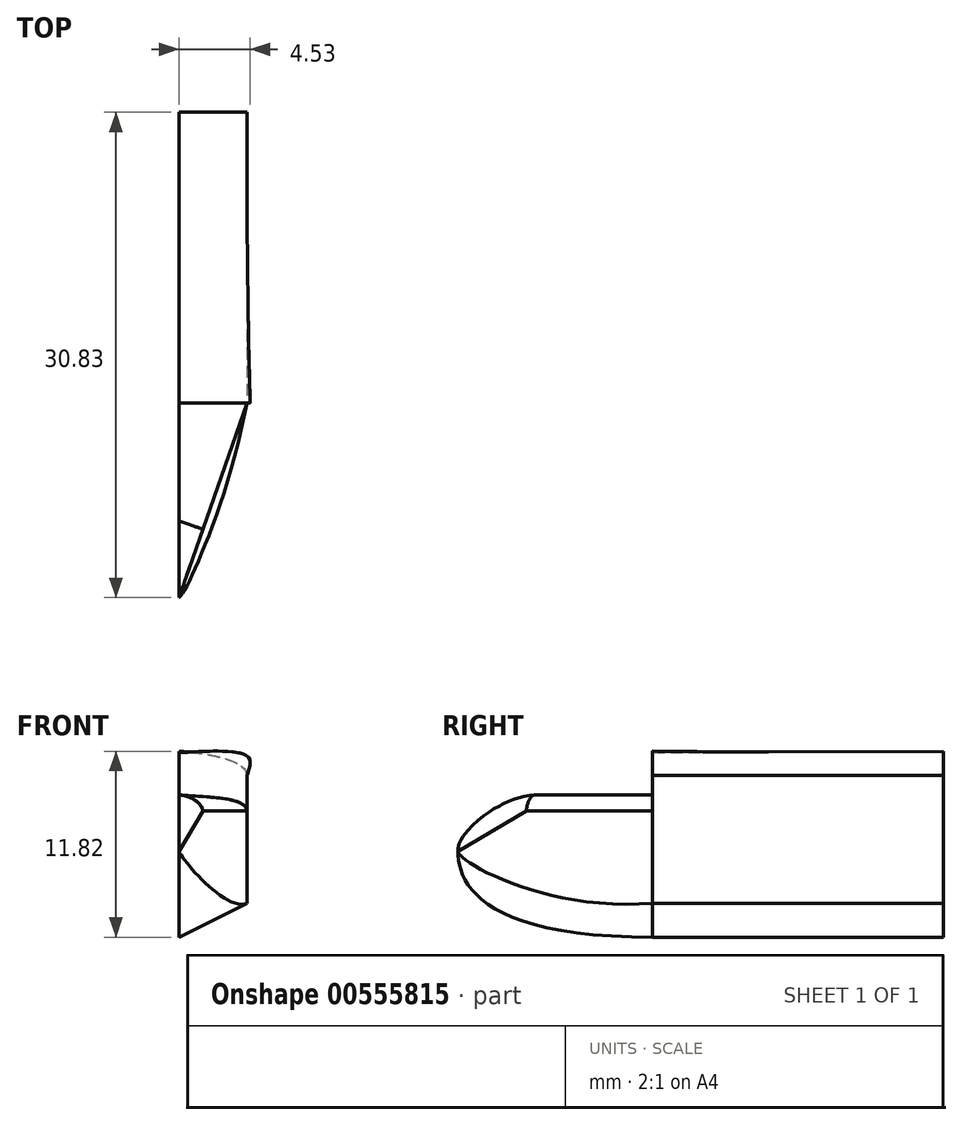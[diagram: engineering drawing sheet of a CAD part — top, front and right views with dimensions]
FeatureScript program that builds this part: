
annotation { "Feature Type Name" : "Feature", "Feature Type Description" : "" }
export const myFeature = defineFeature(function(context is Context, id is Id, definition is map)
    precondition{}
    {
        {
            var Q0;
            Q0=qCreatedBy(makeId("Right.planeOp"),FACE);
            var sketch = newSketch(context, id + "F0", { "sketchPlane" : qUnion([Q0])});
            skLineSegment(sketch, "E0.bottom", {"start": v(-49.13, 14.56) * mm, "end": v(-30.67, 14.56) * mm});
            skLineSegment(sketch, "E0.top", {"start": v(-49.13, 2.76) * mm, "end": v(-30.67, 2.76) * mm});
            skLineSegment(sketch, "E0.left", {"start": v(-49.13, 14.56) * mm, "end": v(-49.13, 2.76) * mm});
            skLineSegment(sketch, "E0.right", {"start": v(-30.67, 14.56) * mm, "end": v(-30.67, 2.76) * mm});
            skLineSegment(sketch, "E1", {"start": v(32.77, 35.45) * mm, "end": v(32.77, -92.3) * mm, "construction": true});
            skLineSegment(sketch, "E2.bottom", {"start": v(32.77, 35.45) * mm, "end": v(-64.37, 35.45) * mm, "construction": true});
            skLineSegment(sketch, "E2.top", {"start": v(32.77, -92.3) * mm, "end": v(-64.37, -92.3) * mm, "construction": true});
            skLineSegment(sketch, "E2.right", {"start": v(-64.37, 35.45) * mm, "end": v(-64.37, -92.3) * mm, "construction": true});
            skLineSegment(sketch, "E3", {"start": v(-49.13, 2.76) * mm, "end": v(-49.13, -2.43) * mm, "construction": true});
            skLineSegment(sketch, "E4", {"start": v(-30.62, 8.23) * mm, "end": v(-47.08, 8.23) * mm, "construction": true});
            skLineSegment(sketch, "E5", {"start": v(-47.08, 8.23) * mm, "end": v(-50.1, 8.23) * mm, "construction": true});
            skLineSegment(sketch, "E6", {"start": v(-50.1, 8.23) * mm, "end": v(-50.1, -2.75) * mm, "construction": true});
            skLineSegment(sketch, "E7", {"start": v(-50.1, 8.23) * mm, "end": v(-53.9, 8.23) * mm, "construction": true});
            skLineSegment(sketch, "E8", {"start": v(-53.9, 8.23) * mm, "end": v(-53.9, -2.7) * mm, "construction": true});
            skLineSegment(sketch, "E9", {"start": v(-53.9, 8.23) * mm, "end": v(-56.62, 8.23) * mm, "construction": true});
            skLineSegment(sketch, "E10", {"start": v(-56.62, 8.23) * mm, "end": v(-59.33, 8.23) * mm, "construction": true});
            skLineSegment(sketch, "E11", {"start": v(-59.33, 8.23) * mm, "end": v(-59.33, -1.53) * mm, "construction": true});
            skLineSegment(sketch, "E12", {"start": v(-56.62, 8.23) * mm, "end": v(-56.62, -1.94) * mm, "construction": true});
            skLineSegment(sketch, "E13", {"start": v(-59.33, 8.23) * mm, "end": v(-61.5, 8.23) * mm, "construction": true});
            skFitSpline(sketch, "E14", {"points": [v(-61.5, 8.23) * mm, v(-49.13, 2.76) * mm], "startDerivative": vector(0, -6.22) * mm, "endDerivative": vector(32.48, 0) * mm});
            skLineSegment(sketch, "E15", {"start": v(-56.62, 11.8) * mm, "end": v(-49.13, 11.8) * mm});
            skLineSegment(sketch, "E16", {"start": v(-56.62, 8.23) * mm, "end": v(-56.62, 11.8) * mm, "construction": true});
            skFitSpline(sketch, "E17", {"points": [v(-56.62, 11.8) * mm, v(-61.5, 8.23) * mm], "startDerivative": vector(-5.3, 0) * mm, "endDerivative": vector(0, -4.44) * mm});
            skSolve(sketch);
        }
        {
            var Q0;
            Q0=qCreatedBy(makeId("Front.planeOp"),FACE);
            var Q1;
            Q1=sQuery(id+"F0.wireOp",VERTEX,"E0.top.end");
            cPlane(context, id + "F1", {"entities" : qUnion([Q0, Q1]), "cplaneType" : CPlaneType.PLANE_POINT, "offset" : 25 * mm, "width" : 150 * mm, "height" : 150 * mm});
        }
        {
            var Q0;
            Q0=qCreatedBy(id+"F1.planeOp",FACE);
            var sketch = newSketch(context, id + "F2", { "sketchPlane" : qUnion([Q0])});
            skLineSegment(sketch, "E18.0", {"start": v(0, 14.56) * mm, "end": v(0, 2.76) * mm, "construction": true});
            skFitSpline(sketch, "E19", {"points": [v(0, 14.56) * mm, v(4.32, 13.04) * mm], "startDerivative": vector(1.52, 0) * mm, "endDerivative": vector(0, -3.7) * mm});
            skLineSegment(sketch, "E20", {"start": v(4.32, 13.04) * mm, "end": v(4.32, 4.92) * mm});
            skLineSegment(sketch, "E21", {"start": v(4.32, 4.92) * mm, "end": v(0, 2.76) * mm});
            skLineSegment(sketch, "E22", {"start": v(4.32, 4.92) * mm, "end": v(0, 4.92) * mm, "construction": true});
            skSolve(sketch);
        }
        {
            var Q0;
            Q0=sQuery(id+"F0.wireOp",EDGE,"E0.left");
            cPoint(context, id + "F3", {"entities" : qUnion([Q0]), "parameter" : 0.5});
        }
        {
            var Q0;
            Q0=qCreatedBy(makeId("Front.planeOp"),FACE);
            var Q1;
            Q1 = qCreatedBy(id + "F3" ,VERTEX);
            cPlane(context, id + "F4", {"entities" : qUnion([Q0, Q1]), "cplaneType" : CPlaneType.PLANE_POINT, "offset" : 25 * mm, "width" : 150 * mm, "height" : 150 * mm});
        }
        {
            var Q0;
            Q0=qCreatedBy(id+"F4.planeOp",FACE);
            var sketch = newSketch(context, id + "F5", { "sketchPlane" : qUnion([Q0])});
            skLineSegment(sketch, "E23.0", {"start": v(4.32, 4.92) * mm, "end": v(0, 2.76) * mm});
            skLineSegment(sketch, "E24.0", {"start": v(4.32, 13.04) * mm, "end": v(4.32, 4.92) * mm});
            skFitSpline(sketch, "E25.0", {"points": [v(0, 14.51) * mm, v(0.5, 14.51) * mm, v(4.32, 14.27) * mm, v(4.32, 13.04) * mm]});
            skSolve(sketch);
        }
        {
            var Q0;
            Q0 = qSketchRegion(id + "F2", true);
            var Q1;
            Q1 = qSketchRegion(id + "F5", true);
            var Q2;
            Q2 = qConstructionFilter(qBodyType(qCreatedBy(id + "F2" ,EDGE), BodyType.WIRE), ConstructionObject.NO);
            var Q3;
            Q3 = qConstructionFilter(qBodyType(qCreatedBy(id + "F5" ,EDGE), BodyType.WIRE), ConstructionObject.NO);
            loft(context, id + "F6", {"bodyType" : ToolBodyType.SURFACE, "sheetProfilesArray" : [{ "sheetProfileEntities" : qUnion([Q0]) }, { "sheetProfileEntities" : qUnion([Q1]) }], "wireProfilesArray" : [{ "wireProfileEntities" : qUnion([Q2]) }, { "wireProfileEntities" : qUnion([Q3]) }]});
        }
        {
            var Q0;
            Q0=qCreatedBy(makeId("Front.planeOp"),FACE);
            var Q1;
            Q1=sQuery(id+"F0.wireOp",VERTEX,"E7.start");
            cPlane(context, id + "F7", {"entities" : qUnion([Q0, Q1]), "cplaneType" : CPlaneType.PLANE_POINT, "offset" : 25 * mm, "width" : 150 * mm, "height" : 150 * mm});
        }
        {
            var Q0;
            Q0=makeQuery(id+"F6.opLoft","MID_CAP_VERTEX",VERTEX,{"disambiguationData":[OSD([sQuery(id+"F5.wireOp",VERTEX,"E24.0.end")])],"capPos":1.0});
            var Q1;
            Q1=sQuery(id+"F0.wireOp",VERTEX,"E14.0.internal");
            var Q2;
            Q2=sQuery(id+"F0.wireOp",VERTEX,"E0.left.start");
            cPlane(context, id + "F8", {"entities" : qUnion([Q0, Q1, Q2]), "cplaneType" : CPlaneType.THREE_POINT, "offset" : 25 * mm, "width" : 150 * mm, "height" : 150 * mm});
        }
        {
            var Q0;
            Q0=qCreatedBy(id+"F8.planeOp",FACE);
            var sketch = newSketch(context, id + "F9", { "sketchPlane" : qUnion([Q0])});
            skPoint(sketch, "E26.0", {"position": v(-59.5, 7.5) * mm});
            skPoint(sketch, "E27.0", {"position": v(-46.87, 2.73) * mm});
            skFitSpline(sketch, "E28", {"points": [v(-59.5, 7.5) * mm, v(-46.87, 2.73) * mm], "startDerivative": vector(0, -2.26) * mm, "endDerivative": vector(20.63, 0) * mm});
            skSolve(sketch);
        }
        {
            var Q0;
            Q0=sQuery(id+"F9.wireOp",EDGE,"E28");
            var Q1;
            Q1=sQuery(id+"F0.wireOp",EDGE,"E14");
            loft(context, id + "F10", {"bodyType" : ToolBodyType.SURFACE, "wireProfilesArray" : [{ "wireProfileEntities" : qUnion([Q0]) }, { "wireProfileEntities" : qUnion([Q1]) }]});
        }
        {
            var Q0;
            Q0=qCreatedBy(id+"F4.planeOp",FACE);
            var sketch = newSketch(context, id + "F11", { "sketchPlane" : qUnion([Q0])});
            skPoint(sketch, "E29.0", {"position": v(0, 11.8) * mm});
            skLineSegment(sketch, "E30.0", {"start": v(4.32, 4.92) * mm, "end": v(4.32, 13.04) * mm, "construction": true});
            skLineSegment(sketch, "E31", {"start": v(4.32, 4.92) * mm, "end": v(4.32, 10.79) * mm});
            skFitSpline(sketch, "E32", {"points": [v(0, 11.8) * mm, v(4.32, 10.79) * mm], "startDerivative": vector(5.4, -0.45) * mm, "endDerivative": vector(0, -2.65) * mm});
            skSolve(sketch);
        }
        {
            var Q0;
            Q0=sQuery(id+"F11.wireOp",VERTEX,"E32.1.internal");
            var Q1;
            Q1=sQuery(id+"F0.wireOp",VERTEX,"E13.end");
            var Q2;
            Q2=sQuery(id+"F11.wireOp",VERTEX,"E30.0.start");
            cPlane(context, id + "F12", {"entities" : qUnion([Q0, Q1, Q2]), "cplaneType" : CPlaneType.THREE_POINT, "offset" : 25 * mm, "width" : 150 * mm, "height" : 150 * mm});
        }
        {
            var Q0;
            Q0=qCreatedBy(id+"F12.planeOp",FACE);
            var sketch = newSketch(context, id + "F13", { "sketchPlane" : qUnion([Q0])});
            skLineSegment(sketch, "E33.0", {"start": v(53.46, 8.23) * mm, "end": v(53.46, 11.8) * mm, "construction": true});
            skPoint(sketch, "E34.0", {"position": v(44.96, 10.79) * mm});
            skPoint(sketch, "E35.0", {"position": v(58.06, 8.23) * mm});
            skFitSpline(sketch, "E36.0", {"points": [v(58.06, 8.23) * mm, v(57.96, 7.54) * mm, v(51.74, 4.35) * mm, v(44.96, 4.92) * mm]});
            skLineSegment(sketch, "E37.0", {"start": v(44.96, 4.92) * mm, "end": v(44.96, 10.79) * mm});
            skLineSegment(sketch, "E38", {"start": v(44.96, 10.79) * mm, "end": v(53.46, 10.79) * mm});
            skLineSegment(sketch, "E39", {"start": v(53.46, 10.79) * mm, "end": v(58.06, 8.23) * mm});
            skSolve(sketch);
        }
        {
            var Q0;
            Q0=sQuery(id+"F0.wireOp",VERTEX,"E15.start");
            var Q1;
            Q1=sQuery(id+"F0.wireOp",VERTEX,"E10.start");
            var Q2;
            Q2=sQuery(id+"F13.wireOp",VERTEX,"E39.start");
            cPlane(context, id + "F14", {"entities" : qUnion([Q0, Q1, Q2]), "cplaneType" : CPlaneType.THREE_POINT, "offset" : 25 * mm, "width" : 150 * mm, "height" : 150 * mm});
        }
        {
            var Q0;
            Q0=qCreatedBy(id+"F14.planeOp",FACE);
            var sketch = newSketch(context, id + "F15", { "sketchPlane" : qUnion([Q0])});
            skPoint(sketch, "E40.0", {"position": v(-18.66, 11.8) * mm});
            skPoint(sketch, "E41.0", {"position": v(-20.27, 10.79) * mm});
            skFitSpline(sketch, "E42.0", {"points": [v(-16.2, 11.8) * mm, v(-17.9, 11.65) * mm, v(-20.27, 11.67) * mm, v(-20.27, 10.79) * mm], "construction": true});
            skFitSpline(sketch, "E43", {"points": [v(-18.66, 11.8) * mm, v(-20.27, 10.79) * mm], "startDerivative": vector(-2.34, 0) * mm, "endDerivative": vector(0, -1.3) * mm});
            skSolve(sketch);
        }
        {
            var Q0;
            Q0=sQuery(id+"F15.wireOp",EDGE,"E43");
            var Q1;
            Q1=sQuery(id+"F11.wireOp",EDGE,"E32");
            loft(context, id + "F16", {"bodyType" : ToolBodyType.SURFACE, "wireProfilesArray" : [{ "wireProfileEntities" : qUnion([Q0]) }, { "wireProfileEntities" : qUnion([Q1]) }]});
        }
        {
            var Q0;
            Q0=makeQuery(id+"F16.opLoft","MID_CAP_EDGE",EDGE,{"disambiguationData":[OSD([sQuery(id+"F15.wireOp",VERTEX,"E43.start"),sQuery(id+"F15.wireOp",VERTEX,"E43.end"),sQuery(id+"F15.wireOp",EDGE,"E43")])],"capPos":0.0});
            var Q1;
            Q1=sQuery(id+"F13.wireOp",VERTEX,"E35.0");
            var Q2;
            Q2=sQuery(id+"F0.wireOp",EDGE,"E17");
            loft(context, id + "F17", {"bodyType" : ToolBodyType.SURFACE, "addGuides" : true, "wireProfilesArray" : [{ "wireProfileEntities" : qUnion([Q0]) }, { "wireProfileEntities" : qUnion([Q1]) }], "guidesArray" : [{ "guideEntities" : qUnion([Q2]), "guideDerivativeType" : LoftGuideDerivativeType.DEFAULT, "guideDerivativeMagnitude" : 1 }]});
        }
        {
            var Q0;
            Q0=makeQuery(id+"F10.opLoft","MID_CAP_EDGE",EDGE,{"disambiguationData":[OSD([sQuery(id+"F9.wireOp",VERTEX,"E28.start"),sQuery(id+"F9.wireOp",VERTEX,"E28.end"),sQuery(id+"F9.wireOp",EDGE,"E28")])],"capPos":0.0});
            var Q1;
            Q1=makeQuery(id+"F16.opLoft","SWEPT_EDGE",EDGE,{"disambiguationData":[OSD([sQuery(id+"F11.wireOp",VERTEX,"E32.end"),sQuery(id+"F15.wireOp",VERTEX,"E43.end")])]});
            loft(context, id + "F18", {"bodyType" : ToolBodyType.SURFACE, "wireProfilesArray" : [{ "wireProfileEntities" : qUnion([Q0]) }, { "wireProfileEntities" : qUnion([Q1]) }]});
        }
        {
            var Q0;
            Q0=makeQuery(id+"F6.opLoft","MID_CAP_EDGE",EDGE,{"disambiguationData":[OSD([sQuery(id+"F5.wireOp",VERTEX,"E25.0.start"),sQuery(id+"F5.wireOp",VERTEX,"E25.0.end"),sQuery(id+"F5.wireOp",EDGE,"E25.0")])],"capPos":1.0});
            var Q1;
            Q1=makeQuery(id+"F16.opLoft","MID_CAP_EDGE",EDGE,{"disambiguationData":[OSD([sQuery(id+"F11.wireOp",VERTEX,"E32.start"),sQuery(id+"F11.wireOp",VERTEX,"E32.end"),sQuery(id+"F11.wireOp",EDGE,"E32")])],"capPos":1.0});
            loft(context, id + "F19", {"bodyType" : ToolBodyType.SURFACE, "wireProfilesArray" : [{ "wireProfileEntities" : qUnion([Q0]) }, { "wireProfileEntities" : qUnion([Q1]) }]});
        }
        {
            var Q0;
            Q0=makeQuery(id+"F6.opLoft","MID_CAP_EDGE",EDGE,{"disambiguationData":[OSD([sQuery(id+"F2.wireOp",VERTEX,"E19.start"),sQuery(id+"F2.wireOp",VERTEX,"E20.start"),sQuery(id+"F2.wireOp",EDGE,"E19")])],"capPos":0.0});
            var Q1;
            Q1=makeQuery(id+"F6.opLoft","MID_CAP_EDGE",EDGE,{"disambiguationData":[OSD([sQuery(id+"F2.wireOp",VERTEX,"E21.start"),sQuery(id+"F2.wireOp",VERTEX,"E21.end"),sQuery(id+"F2.wireOp",EDGE,"E21")])],"capPos":0.0});
            var Q2;
            Q2=sQuery(id+"F0.wireOp",EDGE,"E0.right");
            var Q3;
            Q3=makeQuery(id+"F6.opLoft","MID_CAP_EDGE",EDGE,{"disambiguationData":[OSD([sQuery(id+"F2.wireOp",VERTEX,"E20.start"),sQuery(id+"F2.wireOp",VERTEX,"E21.start"),sQuery(id+"F2.wireOp",EDGE,"E20")])],"capPos":0.0});
            loft(context, id + "F20", {"bodyType" : ToolBodyType.SURFACE, "addGuides" : true, "wireProfilesArray" : [{ "wireProfileEntities" : qUnion([Q0]) }, { "wireProfileEntities" : qUnion([Q1]) }], "guidesArray" : [{ "guideEntities" : qUnion([Q2]), "guideDerivativeType" : LoftGuideDerivativeType.DEFAULT, "guideDerivativeMagnitude" : 1 }, { "guideEntities" : qUnion([Q3]), "guideDerivativeType" : LoftGuideDerivativeType.DEFAULT, "guideDerivativeMagnitude" : 1 }]});
        }
    });
